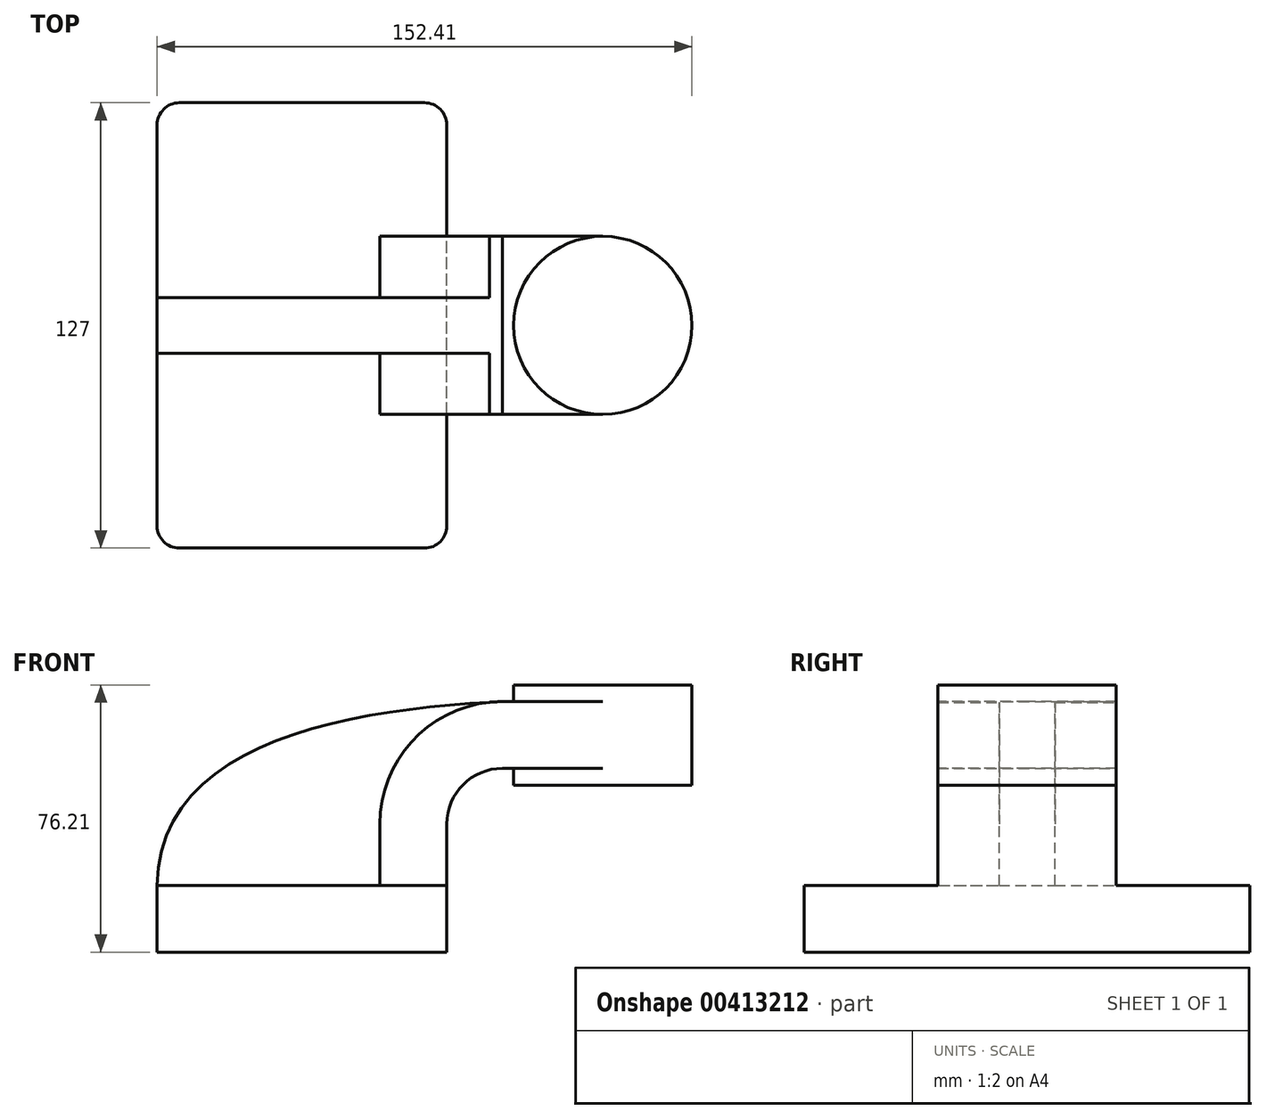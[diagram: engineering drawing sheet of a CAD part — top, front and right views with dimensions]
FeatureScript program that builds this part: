
annotation { "Feature Type Name" : "Feature", "Feature Type Description" : "" }
export const myFeature = defineFeature(function(context is Context, id is Id, definition is map)
    precondition{}
    {
        {
            var Q0;
            Q0=qCreatedBy(makeId("Front.planeOp"),FACE);
            var sketch = newSketch(context, id + "F0", { "sketchPlane" : qUnion([Q0])});
            skLineSegment(sketch, "E0.bottom", {"start": v(41.27, 9.53) * mm, "end": v(-41.28, 9.53) * mm});
            skLineSegment(sketch, "E0.top", {"start": v(41.28, -9.52) * mm, "end": v(-41.27, -9.52) * mm});
            skLineSegment(sketch, "E0.left", {"start": v(41.28, 9.53) * mm, "end": v(41.28, -9.52) * mm});
            skLineSegment(sketch, "E0.right", {"start": v(-41.28, 9.53) * mm, "end": v(-41.27, -9.52) * mm});
            skPoint(sketch, "E0.middle", {"position": v(0, 0) * mm});
            skLineSegment(sketch, "E1.bottom", {"start": v(60.33, 38.1) * mm, "end": v(111.12, 38.1) * mm});
            skLineSegment(sketch, "E1.top", {"start": v(60.33, 66.68) * mm, "end": v(111.12, 66.68) * mm});
            skLineSegment(sketch, "E1.left", {"start": v(60.33, 38.1) * mm, "end": v(60.32, 66.67) * mm});
            skLineSegment(sketch, "E1.right", {"start": v(111.12, 38.1) * mm, "end": v(111.12, 66.68) * mm});
            skPoint(sketch, "E1.middle", {"position": v(85.72, 52.39) * mm});
            skLineSegment(sketch, "E2", {"start": v(41.27, 9.53) * mm, "end": v(41.27, 27) * mm});
            skArc(sketch, "E3", {"start": v(41.27, 27) * mm, "mid": v(45.92, 38.23) * mm, "end": v(57.15, 42.88) * mm});
            skLineSegment(sketch, "E4", {"start": v(57.15, 42.88) * mm, "end": v(98.1, 42.88) * mm});
            skLineSegment(sketch, "E5.0", {"start": v(57.15, 61.93) * mm, "end": v(98.1, 61.93) * mm});
            skArc(sketch, "E5.1", {"start": v(22.23, 27) * mm, "mid": v(32.45, 51.7) * mm, "end": v(57.15, 61.93) * mm});
            skLineSegment(sketch, "E5.2", {"start": v(22.22, 9.53) * mm, "end": v(22.22, 27) * mm});
            skLineSegment(sketch, "E6", {"start": v(85.72, 38.1) * mm, "end": v(85.72, 66.68) * mm});
            skFitSpline(sketch, "E7", {"points": [v(-41.28, 9.52) * mm, v(57.15, 61.93) * mm], "startDerivative": vector(1.5, 123.65) * mm, "endDerivative": vector(130.45, 6.32) * mm});
            skSolve(sketch);
        }
        {
            var Q0;
            Q0=makeQuery(id+"F0.imprint","IMPRINT",FACE,{"disambiguationData":[TD([[makeQuery(id+"F0.imprint","IMPRINT",EDGE,{"derivedFrom":sQuery(id+"F0.wireOp",EDGE,"E0.top")}),-1.0]])]});
            extrude(context, id + "F1", {"entities" : qUnion([Q0]), "endBound" : BoundingType.SYMMETRIC, "depth" : 127 * mm});
        }
        {
            var Q0;
            {var subQ1=sQuery(id+"F0.wireOp",EDGE,"E2");Q0=makeQuery(id+"F0.imprint","IMPRINT",FACE,{"disambiguationData":[TD([[makeQuery(id+"F0.imprint","IMPRINT",EDGE,{"derivedFrom":subQ1}),1.0]])]});}
            var Q1;
            {var subQ0=sQuery(id+"F0.wireOp",EDGE,"E4");var subQ1=sQuery(id+"F0.wireOp",EDGE,"E1.left");var subQ2=makeQuery(id+"F0.imprint","INTERSECT",VERTEX,{"derivedFrom":[subQ1,subQ0]});Q1=makeQuery(id+"F0.imprint","IMPRINT",FACE,{"disambiguationData":[TD([[makeQuery(id+"F0.imprint","IMPRINT",EDGE,{"disambiguationData":[TD([[subQ2,-1.0]])],"derivedFrom":subQ1}),-1.0]])]});}
            extrude(context, id + "F2", {"entities" : qUnion([Q0, Q1]), "operationType" : NewBodyOperationType.ADD, "endBound" : BoundingType.SYMMETRIC, "depth" : 50.8 * mm});
        }
        {
            var Q0;
            {var subQ3=sQuery(id+"F0.wireOp",EDGE,"E5.2");Q0=makeQuery(id+"F0.imprint","IMPRINT",FACE,{"disambiguationData":[TD([[makeQuery(id+"F0.imprint","IMPRINT",EDGE,{"derivedFrom":subQ3}),1.0]])]});}
            extrude(context, id + "F3", {"entities" : qUnion([Q0]), "operationType" : NewBodyOperationType.ADD, "endBound" : BoundingType.SYMMETRIC, "depth" : 15.88 * mm});
        }
        {
            var Q0;
            {var subQ4=sQuery(id+"F0.wireOp",EDGE,"E1.right");Q0=makeQuery(id+"F0.imprint","IMPRINT",FACE,{"disambiguationData":[TD([[makeQuery(id+"F0.imprint","IMPRINT",EDGE,{"derivedFrom":subQ4}),1.0]])]});}
            var Q1;
            Q1=sQuery(id+"F0.wireOp",EDGE,"E6");
            revolve(context, id + "F4", {"operationType" : NewBodyOperationType.ADD, "entities" : qUnion([Q0]), "axis" : qUnion([Q1]), "revolveType" : RevolveType.FULL});
        }
        {
            var Q0;
            Q0=makeQuery(id+"F1.opExtrude","CAP_EDGE",EDGE,{"disambiguationData":[OSD([sQuery(id+"F0.wireOp",EDGE,"E0.left")])],"isStart":false});
            var Q1;
            Q1=makeQuery(id+"F1.opExtrude","CAP_EDGE",EDGE,{"disambiguationData":[OSD([sQuery(id+"F0.wireOp",EDGE,"E0.right")])],"isStart":true});
            var Q2;
            Q2=makeQuery(id+"F1.opExtrude","CAP_EDGE",EDGE,{"disambiguationData":[OSD([sQuery(id+"F0.wireOp",EDGE,"E0.right")])],"isStart":false});
            var Q3;
            Q3=makeQuery(id+"F1.opExtrude","CAP_EDGE",EDGE,{"disambiguationData":[OSD([sQuery(id+"F0.wireOp",EDGE,"E0.left")])],"isStart":true});
            fillet(context, id + "F5", {"entities" : qUnion([Q0, Q1, Q2, Q3]), "radius" : 6.35 * mm, "tangentPropagation" : true, "allowEdgeOverflow" : false});
        }
    });
